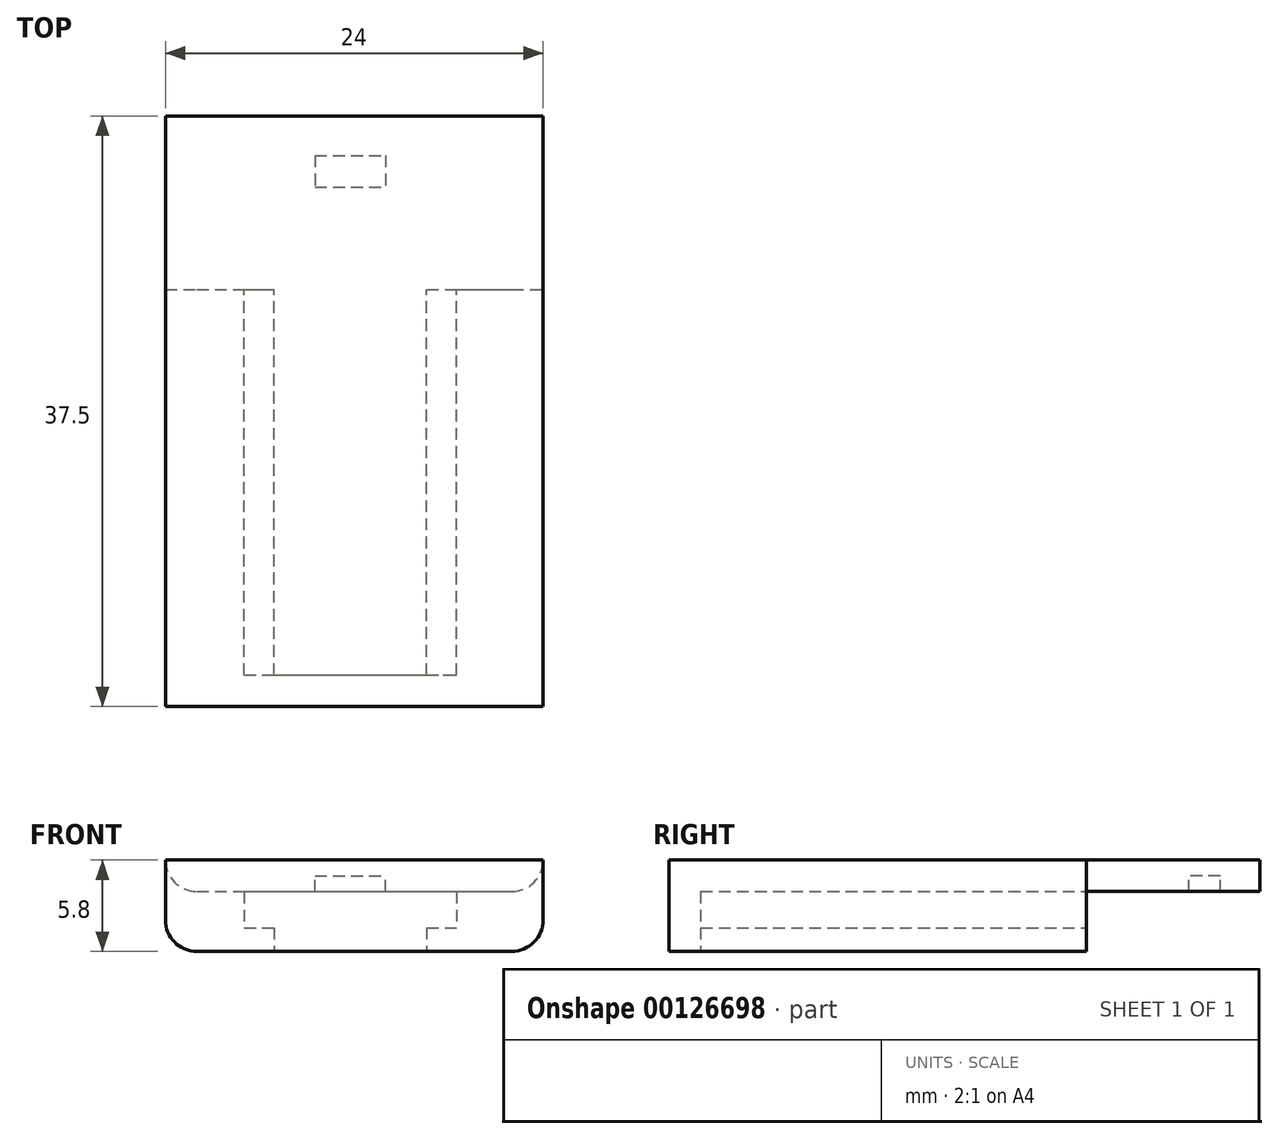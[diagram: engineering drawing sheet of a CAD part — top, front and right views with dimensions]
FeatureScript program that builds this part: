
annotation { "Feature Type Name" : "Feature", "Feature Type Description" : "" }
export const myFeature = defineFeature(function(context is Context, id is Id, definition is map)
    precondition{}
    {
        {
            var Q0;
            Q0=qCreatedBy(makeId("Front.planeOp"),FACE);
            var sketch = newSketch(context, id + "F0", { "sketchPlane" : qUnion([Q0])});
            skLineSegment(sketch, "E0.bottom", {"start": v(-6.75, 4.5) * mm, "end": v(-3.2, 4.5) * mm});
            skLineSegment(sketch, "E0.top", {"start": v(-6.75, 2.2) * mm, "end": v(-3.45, 2.2) * mm});
            skLineSegment(sketch, "E0.left", {"start": v(-6.75, 4.5) * mm, "end": v(-6.75, 2.2) * mm});
            skLineSegment(sketch, "E0.right", {"start": v(6.75, 4.5) * mm, "end": v(6.75, 2.2) * mm});
            skPoint(sketch, "E0.middle", {"position": v(0, 3.35) * mm});
            skLineSegment(sketch, "E1", {"start": v(4.85, 4.5) * mm, "end": v(4.85, 0) * mm});
            skLineSegment(sketch, "E2", {"start": v(-7.46, 0) * mm, "end": v(7.46, 0) * mm});
            skLineSegment(sketch, "E3.MirrorCS", {"start": v(-4.85, 4.5) * mm, "end": v(-4.85, 0) * mm});
            skLineSegment(sketch, "E4.trimOffspring", {"start": v(3.2, 4.5) * mm, "end": v(6.75, 4.5) * mm});
            skLineSegment(sketch, "E5.trimOffspring", {"start": v(3.45, 2.2) * mm, "end": v(6.75, 2.2) * mm});
            skLineSegment(sketch, "E6.top", {"start": v(-7.46, -2.58) * mm, "end": v(7.46, -2.58) * mm});
            skLineSegment(sketch, "E6.left", {"start": v(-7.46, 0) * mm, "end": v(-7.46, -2.58) * mm});
            skLineSegment(sketch, "E6.right", {"start": v(7.46, 0) * mm, "end": v(7.46, -2.58) * mm});
            skPoint(sketch, "E6.middle", {"position": v(0, -1.3) * mm});
            skLineSegment(sketch, "E7.bottom", {"start": v(-11.75, 6.5) * mm, "end": v(12.25, 6.5) * mm});
            skLineSegment(sketch, "E7.top", {"start": v(-11.75, 0.7) * mm, "end": v(-3.45, 0.7) * mm});
            skLineSegment(sketch, "E7.left", {"start": v(-11.75, 6.5) * mm, "end": v(-11.75, 0.7) * mm});
            skLineSegment(sketch, "E7.right", {"start": v(12.25, 6.5) * mm, "end": v(12.25, 0.7) * mm});
            skLineSegment(sketch, "E8.trimOffspring", {"start": v(3.45, 0.7) * mm, "end": v(12.25, 0.7) * mm});
            skLineSegment(sketch, "E9", {"start": v(-3.2, 4.5) * mm, "end": v(3.2, 4.5) * mm});
            skSolve(sketch);
        }
        {
            var Q0;
            {var subQ15=sQuery(id+"F0.wireOp",EDGE,"E0.left");Q0=makeQuery(id+"F0.imprint","IMPRINT",FACE,{"disambiguationData":[TD([[makeQuery(id+"F0.imprint","IMPRINT",EDGE,{"derivedFrom":subQ15}),-1.0]])]});}
            extrude(context, id + "F1", {"entities" : qUnion([Q0]), "depth" : 24.5 * mm});
        }
        {
            var Q0;
            Q0=makeQuery(id+"F1.opExtrude","CAP_FACE",FACE,{"disambiguationData":[OSD([sQuery(id+"F0.wireOp",EDGE,"E0.bottom"),sQuery(id+"F0.wireOp",EDGE,"E0.top"),sQuery(id+"F0.wireOp",EDGE,"E0.left"),sQuery(id+"F0.wireOp",EDGE,"E0.right"),sQuery(id+"F0.wireOp",EDGE,"S1AUJSAj-lBYP-Ti23-zWH8-DRC2IawmwYyc"),sQuery(id+"F0.wireOp",EDGE,"0b6ff6ab-89a0-4641-988e-e83ad78c142a0.MirrorCS"),sQuery(id+"F0.wireOp",EDGE,"E4.trimOffspring"),sQuery(id+"F0.wireOp",EDGE,"E5.trimOffspring"),sQuery(id+"F0.wireOp",EDGE,"E7.bottom"),sQuery(id+"F0.wireOp",EDGE,"E7.top"),sQuery(id+"F0.wireOp",EDGE,"E7.left"),sQuery(id+"F0.wireOp",EDGE,"E7.right"),sQuery(id+"F0.wireOp",EDGE,"E8.trimOffspring"),sQuery(id+"F0.wireOp",EDGE,"E9")])],"isStart":false});
            var sketch = newSketch(context, id + "F2", { "sketchPlane" : qUnion([Q0])});
            skLineSegment(sketch, "E10.bottom", {"start": v(-11.75, 6.5) * mm, "end": v(12.25, 6.5) * mm});
            skLineSegment(sketch, "E10.top", {"start": v(-11.75, 0.7) * mm, "end": v(12.25, 0.7) * mm});
            skLineSegment(sketch, "E10.left", {"start": v(-11.75, 6.5) * mm, "end": v(-11.75, 0.7) * mm});
            skLineSegment(sketch, "E10.right", {"start": v(12.25, 6.5) * mm, "end": v(12.25, 0.7) * mm});
            skSolve(sketch);
        }
        {
            var Q0;
            Q0=qSketchRegion(id+"F2",true);
            extrude(context, id + "F3", {"entities" : qUnion([Q0]), "operationType" : NewBodyOperationType.ADD, "depth" : 2 * mm});
        }
        {
            var Q0;
            Q0=makeQuery(id+"F3.boolean.opBoolean","MERGE",FACE,{"derivedFrom":[makeQuery(id+"F1.opExtrude","SWEPT_FACE",FACE,{"disambiguationData":[OSD([sQuery(id+"F0.wireOp",EDGE,"E7.bottom")])]}),makeQuery(id+"F3.opExtrude","SWEPT_FACE",FACE,{"disambiguationData":[OSD([sQuery(id+"F2.wireOp",EDGE,"E10.bottom")])]})]});
            var sketch = newSketch(context, id + "F4", { "sketchPlane" : qUnion([Q0])});
            skLineSegment(sketch, "E11.bottom", {"start": v(-11.75, 0) * mm, "end": v(12.25, 0) * mm});
            skLineSegment(sketch, "E11.top", {"start": v(-11.75, 11) * mm, "end": v(12.25, 11) * mm});
            skLineSegment(sketch, "E11.left", {"start": v(-11.75, 0) * mm, "end": v(-11.75, 11) * mm});
            skLineSegment(sketch, "E11.right", {"start": v(12.25, 0) * mm, "end": v(12.25, 11) * mm});
            skLineSegment(sketch, "E12.bottom", {"start": v(-2.25, 8.5) * mm, "end": v(2.25, 8.5) * mm});
            skLineSegment(sketch, "E12.top", {"start": v(-2.25, 6.5) * mm, "end": v(2.25, 6.5) * mm});
            skLineSegment(sketch, "E12.left", {"start": v(-2.25, 8.5) * mm, "end": v(-2.25, 6.5) * mm});
            skLineSegment(sketch, "E12.right", {"start": v(2.25, 8.5) * mm, "end": v(2.25, 6.5) * mm});
            skPoint(sketch, "E12.middle", {"position": v(0, 7.5) * mm});
            skSolve(sketch);
        }
        {
            var Q0;
            Q0=makeQuery(id+"F4.imprint","IMPRINT",FACE,{"disambiguationData":[TD([[makeQuery(id+"F4.imprint","IMPRINT",EDGE,{"derivedFrom":sQuery(id+"F4.wireOp",EDGE,"E11.bottom")}),1.0]])]});
            extrude(context, id + "F5", {"entities" : qUnion([Q0]), "operationType" : NewBodyOperationType.ADD, "oppositeDirection" : true, "depth" : 2 * mm});
        }
        {
            var Q0;
            Q0=makeQuery(id+"F4.imprint","IMPRINT",FACE,{"disambiguationData":[TD([[makeQuery(id+"F4.imprint","IMPRINT",EDGE,{"derivedFrom":sQuery(id+"F4.wireOp",EDGE,"E12.bottom")}),-1.0]])]});
            extrude(context, id + "F6", {"entities" : qUnion([Q0]), "operationType" : NewBodyOperationType.ADD, "oppositeDirection" : true, "depth" : 1 * mm});
        }
        {
            var Q0;
            Q0=makeQuery(id+"F5.opExtrude","CAP_EDGE",EDGE,{"disambiguationData":[OSD([sQuery(id+"F4.wireOp",EDGE,"E11.left")])],"isStart":false});
            var Q1;
            Q1=makeQuery(id+"F5.opExtrude","CAP_EDGE",EDGE,{"disambiguationData":[OSD([sQuery(id+"F4.wireOp",EDGE,"E11.right")])],"isStart":false});
            var Q2;
            Q2=makeQuery(id+"F3.boolean.opBoolean","MERGE",EDGE,{"derivedFrom":[makeQuery(id+"F1.opExtrude","SWEPT_EDGE",EDGE,{"disambiguationData":[OSD([sQuery(id+"F0.wireOp",EDGE,"E7.top"),sQuery(id+"F0.wireOp",EDGE,"E7.left")])]}),makeQuery(id+"F3.opExtrude","SWEPT_EDGE",EDGE,{"disambiguationData":[OSD([sQuery(id+"F2.wireOp",EDGE,"E10.top"),sQuery(id+"F2.wireOp",EDGE,"E10.left")])]})]});
            var Q3;
            Q3=makeQuery(id+"F3.boolean.opBoolean","MERGE",EDGE,{"derivedFrom":[makeQuery(id+"F1.opExtrude","SWEPT_EDGE",EDGE,{"disambiguationData":[OSD([sQuery(id+"F0.wireOp",EDGE,"E7.right"),sQuery(id+"F0.wireOp",EDGE,"E8.trimOffspring")])]}),makeQuery(id+"F3.opExtrude","SWEPT_EDGE",EDGE,{"disambiguationData":[OSD([sQuery(id+"F2.wireOp",EDGE,"E10.top"),sQuery(id+"F2.wireOp",EDGE,"E10.right")])]})]});
            fillet(context, id + "F7", {"entities" : qUnion([Q0, Q1, Q2, Q3]), "radius" : 2 * mm, "tangentPropagation" : true, "allowEdgeOverflow" : false});
        }
    });
